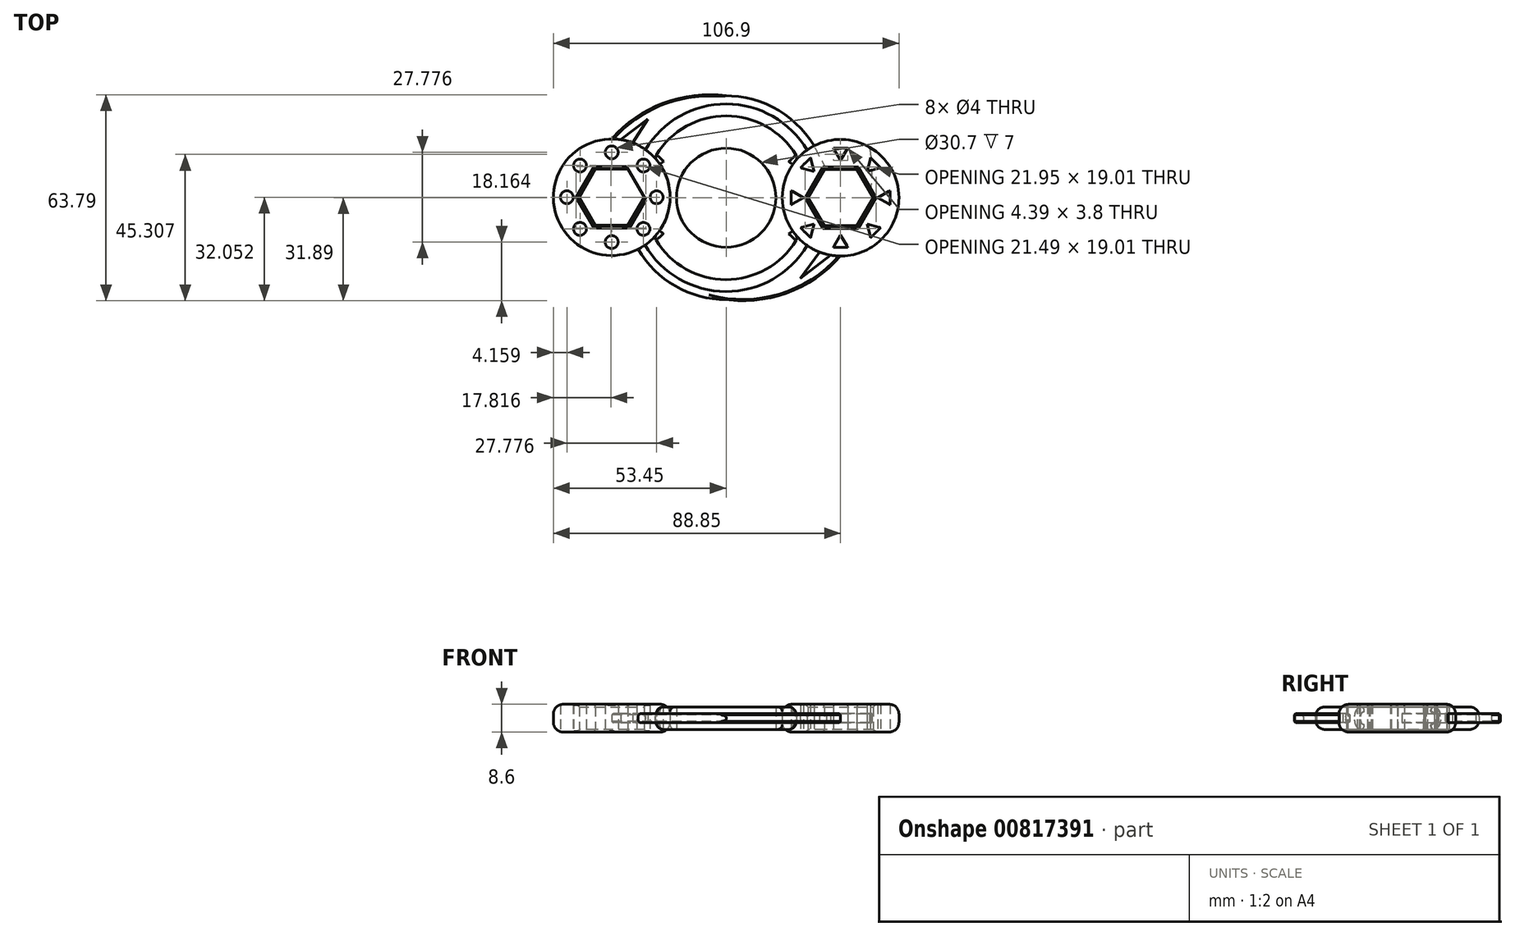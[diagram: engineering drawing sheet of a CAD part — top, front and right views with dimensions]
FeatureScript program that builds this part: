
annotation { "Feature Type Name" : "Feature", "Feature Type Description" : "" }
export const myFeature = defineFeature(function(context is Context, id is Id, definition is map)
    precondition{}
    {
        {
            var Q0;
            Q0=qCreatedBy(makeId("Top.planeOp"),FACE);
            var sketch = newSketch(context, id + "F0", { "sketchPlane" : qUnion([Q0])});
            skCircle(sketch, "E0", {"center": v(0, 0) * mm, "radius": 15.35 * mm});
            skCircle(sketch, "E1", {"center": v(0, 0) * mm, "radius": 25.35 * mm});
            skCircle(sketch, "E2", {"center": v(-35.4, 0.16) * mm, "radius": 10.05 * mm, "construction": true});
            skLineSegment(sketch, "E3.0", {"start": v(-45.45, 0.16) * mm, "end": v(-40.43, -8.54) * mm});
            skLineSegment(sketch, "E3.1", {"start": v(-40.43, 8.87) * mm, "end": v(-45.45, 0.16) * mm});
            skLineSegment(sketch, "E3.3", {"start": v(-25.35, 0.16) * mm, "end": v(-30.38, 8.87) * mm});
            skLineSegment(sketch, "E3.4", {"start": v(-25.35, 0.16) * mm, "end": v(-30.38, -8.54) * mm});
            skLineSegment(sketch, "E3.5", {"start": v(-40.43, -8.54) * mm, "end": v(-30.38, -8.54) * mm});
            skCircle(sketch, "E4.cCircle", {"center": v(35.4, 0) * mm, "radius": 10.05 * mm, "construction": true});
            skLineSegment(sketch, "E4.0", {"start": v(25.35, 0) * mm, "end": v(30.37, 8.7) * mm});
            skLineSegment(sketch, "E4.1", {"start": v(30.38, 8.7) * mm, "end": v(40.42, 8.7) * mm});
            skLineSegment(sketch, "E4.2", {"start": v(40.42, 8.7) * mm, "end": v(45.45, 0) * mm});
            skLineSegment(sketch, "E4.3", {"start": v(45.45, 0) * mm, "end": v(40.43, -8.7) * mm});
            skLineSegment(sketch, "E4.4", {"start": v(40.43, -8.7) * mm, "end": v(30.38, -8.7) * mm});
            skLineSegment(sketch, "E4.5", {"start": v(30.37, -8.7) * mm, "end": v(25.35, 0) * mm});
            skCircle(sketch, "E5", {"center": v(-35.4, 0.16) * mm, "radius": 18.05 * mm});
            skCircle(sketch, "E6", {"center": v(35.4, 0) * mm, "radius": 18.05 * mm});
            skCircle(sketch, "E7", {"center": v(0, 0) * mm, "radius": 31.56 * mm});
            skCircle(sketch, "E8", {"center": v(0, 0) * mm, "radius": 29.06 * mm});
            skLineSegment(sketch, "E9", {"start": v(-40.43, 8.87) * mm, "end": v(-30.38, 8.87) * mm});
            skCircle(sketch, "E10", {"center": v(-35.4, 0.16) * mm, "radius": 14.05 * mm, "construction": true});
            skCircle(sketch, "E11", {"center": v(35.4, 0) * mm, "radius": 14.05 * mm, "construction": true});
            skLineSegment(sketch, "E12.bottom", {"start": v(35.4, 14.05) * mm, "end": v(-35.4, 14.05) * mm, "construction": true});
            skLineSegment(sketch, "E12.top", {"start": v(35.4, -14.05) * mm, "end": v(-35.4, -14.05) * mm, "construction": true});
            skLineSegment(sketch, "E12.left", {"start": v(35.4, 14.05) * mm, "end": v(35.4, -14.05) * mm, "construction": true});
            skLineSegment(sketch, "E12.right", {"start": v(-35.4, 14.05) * mm, "end": v(-35.4, -14.05) * mm, "construction": true});
            skPoint(sketch, "E12.cornerSnap0", {"position": v(35.4, 8.7) * mm});
            skCircle(sketch, "E13", {"center": v(-35.4, 14.05) * mm, "radius": 2 * mm});
            skCircle(sketch, "E14.1.0", {"center": v(-45.22, 9.98) * mm, "radius": 2 * mm});
            skCircle(sketch, "E14.2.0", {"center": v(-49.3, 0.16) * mm, "radius": 2 * mm});
            skCircle(sketch, "E14.3.0", {"center": v(-45.23, -9.66) * mm, "radius": 2 * mm});
            skCircle(sketch, "E14.4.0", {"center": v(-35.4, -13.73) * mm, "radius": 2 * mm});
            skCircle(sketch, "E14.5.0", {"center": v(-25.58, -9.66) * mm, "radius": 2 * mm});
            skCircle(sketch, "E14.6.0", {"center": v(-21.51, 0.16) * mm, "radius": 2 * mm});
            skCircle(sketch, "E14.7.0", {"center": v(-25.58, 9.98) * mm, "radius": 2 * mm});
            skCircle(sketch, "E15.cCircle", {"center": v(35.4, 14.05) * mm, "radius": 1.27 * mm, "construction": true});
            skLineSegment(sketch, "E15.0", {"start": v(33.2, 15.32) * mm, "end": v(37.6, 15.32) * mm});
            skLineSegment(sketch, "E15.1", {"start": v(37.6, 15.32) * mm, "end": v(35.4, 11.52) * mm});
            skLineSegment(sketch, "E15.2", {"start": v(35.4, 11.52) * mm, "end": v(33.2, 15.32) * mm});
            skPoint(sketch, "E15.0.midPoint", {"position": v(35.4, 15.32) * mm});
            skLineSegment(sketch, "E16.1.0", {"start": v(23.02, 9.28) * mm, "end": v(26.12, 12.38) * mm});
            skLineSegment(sketch, "E16.1.1", {"start": v(27.26, 8.14) * mm, "end": v(23.02, 9.28) * mm});
            skLineSegment(sketch, "E16.1.2", {"start": v(26.12, 12.38) * mm, "end": v(27.26, 8.14) * mm});
            skCircle(sketch, "E16.1.3", {"center": v(25.47, 9.93) * mm, "radius": 1.27 * mm, "construction": true});
            skLineSegment(sketch, "E16.2.0", {"start": v(20.08, -2.2) * mm, "end": v(20.08, 2.2) * mm});
            skLineSegment(sketch, "E16.2.1", {"start": v(23.88, 0) * mm, "end": v(20.08, -2.2) * mm});
            skLineSegment(sketch, "E16.2.2", {"start": v(20.08, 2.2) * mm, "end": v(23.88, 0) * mm});
            skCircle(sketch, "E16.2.3", {"center": v(21.35, 0) * mm, "radius": 1.27 * mm, "construction": true});
            skLineSegment(sketch, "E16.3.0", {"start": v(26.12, -12.38) * mm, "end": v(23.02, -9.28) * mm});
            skLineSegment(sketch, "E16.3.1", {"start": v(27.26, -8.14) * mm, "end": v(26.12, -12.38) * mm});
            skLineSegment(sketch, "E16.3.2", {"start": v(23.02, -9.28) * mm, "end": v(27.26, -8.14) * mm});
            skCircle(sketch, "E16.3.3", {"center": v(25.47, -9.93) * mm, "radius": 1.27 * mm, "construction": true});
            skLineSegment(sketch, "E16.4.0", {"start": v(37.6, -15.32) * mm, "end": v(33.2, -15.32) * mm});
            skLineSegment(sketch, "E16.4.1", {"start": v(35.4, -11.52) * mm, "end": v(37.6, -15.32) * mm});
            skLineSegment(sketch, "E16.4.2", {"start": v(33.2, -15.32) * mm, "end": v(35.4, -11.52) * mm});
            skCircle(sketch, "E16.4.3", {"center": v(35.4, -14.05) * mm, "radius": 1.27 * mm, "construction": true});
            skLineSegment(sketch, "E16.5.0", {"start": v(47.78, -9.28) * mm, "end": v(44.68, -12.38) * mm});
            skLineSegment(sketch, "E16.5.1", {"start": v(43.54, -8.14) * mm, "end": v(47.78, -9.28) * mm});
            skLineSegment(sketch, "E16.5.2", {"start": v(44.68, -12.38) * mm, "end": v(43.54, -8.14) * mm});
            skCircle(sketch, "E16.5.3", {"center": v(45.33, -9.93) * mm, "radius": 1.27 * mm, "construction": true});
            skLineSegment(sketch, "E16.6.0", {"start": v(50.72, 2.2) * mm, "end": v(50.72, -2.2) * mm});
            skLineSegment(sketch, "E16.6.1", {"start": v(46.92, 0) * mm, "end": v(50.72, 2.2) * mm});
            skLineSegment(sketch, "E16.6.2", {"start": v(50.72, -2.2) * mm, "end": v(46.92, 0) * mm});
            skCircle(sketch, "E16.6.3", {"center": v(49.45, 0) * mm, "radius": 1.27 * mm, "construction": true});
            skLineSegment(sketch, "E16.7.0", {"start": v(44.68, 12.38) * mm, "end": v(47.78, 9.28) * mm});
            skLineSegment(sketch, "E16.7.1", {"start": v(43.54, 8.14) * mm, "end": v(44.68, 12.38) * mm});
            skLineSegment(sketch, "E16.7.2", {"start": v(47.78, 9.28) * mm, "end": v(43.54, 8.14) * mm});
            skCircle(sketch, "E16.7.3", {"center": v(45.33, 9.93) * mm, "radius": 1.27 * mm, "construction": true});
            skCircle(sketch, "E17", {"center": v(-5.27, -8.1) * mm, "radius": 40 * mm});
            skPoint(sketch, "E17.first.point", {"position": v(-35.4, 18.21) * mm});
            skPoint(sketch, "E17.second.point", {"position": v(0, 31.56) * mm});
            skPoint(sketch, "E17.third.point", {"position": v(-25.3, 26.53) * mm});
            skCircle(sketch, "E18", {"center": v(5.14, 8.11) * mm, "radius": 40 * mm});
            skPoint(sketch, "E18.first.point", {"position": v(35.4, -18.05) * mm});
            skPoint(sketch, "E18.first.point.positionSnap0", {"position": v(35.4, -15.32) * mm});
            skPoint(sketch, "E18.second.point", {"position": v(0, -31.56) * mm});
            skPoint(sketch, "E18.second.point.positionSnap0", {"position": v(0, -14.05) * mm});
            skPoint(sketch, "E18.third.point", {"position": v(-8.62, 45.67) * mm});
            skLineSegment(sketch, "E19", {"start": v(-32.58, 18) * mm, "end": v(-24.21, 24.34) * mm});
            skLineSegment(sketch, "E20", {"start": v(-24.21, 24.34) * mm, "end": v(-28.93, 17.01) * mm});
            skLineSegment(sketch, "E21", {"start": v(28.9, -16.84) * mm, "end": v(22.96, -24.97) * mm});
            skLineSegment(sketch, "E22", {"start": v(22.96, -24.97) * mm, "end": v(32.33, -17.79) * mm});
            skSolve(sketch);
        }
        {
            var Q0;
            {var subQ0=sQuery(id+"F0.wireOp",EDGE,"E7");var subQ4=sQuery(id+"F0.wireOp",EDGE,"E5");var subQ5=makeQuery(id+"F0.imprint","INTERSECT",VERTEX,{"disambiguationData":[OD(0.0)],"derivedFrom":[subQ4,subQ0]});Q0=makeQuery(id+"F0.imprint","IMPRINT",FACE,{"disambiguationData":[TD([[makeQuery(id+"F0.imprint","IMPRINT",EDGE,{"disambiguationData":[TD([[subQ5,-1.0]])],"derivedFrom":subQ4}),1.0]])]});}
            var Q1;
            {var subQ0=sQuery(id+"F0.wireOp",EDGE,"E3.4");Q1=makeQuery(id+"F0.imprint","IMPRINT",FACE,{"disambiguationData":[TD([[makeQuery(id+"F0.imprint","IMPRINT",EDGE,{"derivedFrom":subQ0}),1.0]])]});}
            var Q2;
            {var subQ0=sQuery(id+"F0.wireOp",EDGE,"E5");var subQ1=sQuery(id+"F0.wireOp",EDGE,"E1");var subQ2=makeQuery(id+"F0.imprint","INTERSECT",VERTEX,{"disambiguationData":[OD(0.0)],"derivedFrom":[subQ1,subQ0]});Q2=makeQuery(id+"F0.imprint","IMPRINT",FACE,{"disambiguationData":[TD([[makeQuery(id+"F0.imprint","IMPRINT",EDGE,{"disambiguationData":[TD([[subQ2,-1.0]])],"derivedFrom":subQ0}),1.0]])]});}
            var Q3;
            {var subQ0=sQuery(id+"F0.wireOp",EDGE,"E7");var subQ5=sQuery(id+"F0.wireOp",EDGE,"E5");var subQ6=makeQuery(id+"F0.imprint","INTERSECT",VERTEX,{"disambiguationData":[OD(0.0)],"derivedFrom":[subQ5,subQ0]});Q3=makeQuery(id+"F0.imprint","IMPRINT",FACE,{"disambiguationData":[TD([[makeQuery(id+"F0.imprint","IMPRINT",EDGE,{"disambiguationData":[TD([[subQ6,1.0]])],"derivedFrom":subQ5}),1.0]])]});}
            var Q4;
            {var subQ2=sQuery(id+"F0.wireOp",EDGE,"E5");var subQ5=makeQuery(id+"F0.imprint","INTERSECT",VERTEX,{"derivedFrom":[sQuery(id+"F0.wireOp",EDGE,"E0"),subQ2]});Q4=makeQuery(id+"F0.imprint","IMPRINT",FACE,{"disambiguationData":[TD([[makeQuery(id+"F0.imprint","IMPRINT",EDGE,{"disambiguationData":[TD([[subQ5,-1.0]])],"derivedFrom":subQ2}),1.0]])]});}
            var Q5;
            {var subQ2=sQuery(id+"F0.wireOp",EDGE,"E6");var subQ5=makeQuery(id+"F0.imprint","INTERSECT",VERTEX,{"derivedFrom":[sQuery(id+"F0.wireOp",EDGE,"E0"),subQ2]});Q5=makeQuery(id+"F0.imprint","IMPRINT",FACE,{"disambiguationData":[TD([[makeQuery(id+"F0.imprint","IMPRINT",EDGE,{"disambiguationData":[TD([[subQ5,1.0]])],"derivedFrom":subQ2}),1.0]])]});}
            var Q6;
            {var subQ0=sQuery(id+"F0.wireOp",EDGE,"E5");var subQ1=sQuery(id+"F0.wireOp",EDGE,"E1");var subQ2=makeQuery(id+"F0.imprint","INTERSECT",VERTEX,{"disambiguationData":[OD(1.0)],"derivedFrom":[subQ1,subQ0]});Q6=makeQuery(id+"F0.imprint","IMPRINT",FACE,{"disambiguationData":[TD([[makeQuery(id+"F0.imprint","IMPRINT",EDGE,{"disambiguationData":[TD([[subQ2,1.0]])],"derivedFrom":subQ0}),1.0]])]});}
            var Q7;
            {var subQ1=sQuery(id+"F0.wireOp",EDGE,"E4.2");Q7=makeQuery(id+"F0.imprint","IMPRINT",FACE,{"disambiguationData":[TD([[makeQuery(id+"F0.imprint","IMPRINT",EDGE,{"derivedFrom":subQ1}),1.0]])]});}
            var Q8;
            {var subQ5=sQuery(id+"F0.wireOp",EDGE,"E4.5");Q8=makeQuery(id+"F0.imprint","IMPRINT",FACE,{"disambiguationData":[TD([[makeQuery(id+"F0.imprint","IMPRINT",EDGE,{"derivedFrom":subQ5}),1.0]])]});}
            var Q9;
            {var subQ0=sQuery(id+"F0.wireOp",EDGE,"E7");var subQ5=sQuery(id+"F0.wireOp",EDGE,"E6");var subQ6=makeQuery(id+"F0.imprint","INTERSECT",VERTEX,{"disambiguationData":[OD(1.0)],"derivedFrom":[subQ5,subQ0]});Q9=makeQuery(id+"F0.imprint","IMPRINT",FACE,{"disambiguationData":[TD([[makeQuery(id+"F0.imprint","IMPRINT",EDGE,{"disambiguationData":[TD([[subQ6,1.0]])],"derivedFrom":subQ5}),1.0]])]});}
            var Q10;
            {var subQ0=sQuery(id+"F0.wireOp",EDGE,"E7");var subQ5=sQuery(id+"F0.wireOp",EDGE,"E6");var subQ6=makeQuery(id+"F0.imprint","INTERSECT",VERTEX,{"disambiguationData":[OD(0.0)],"derivedFrom":[subQ5,subQ0]});Q10=makeQuery(id+"F0.imprint","IMPRINT",FACE,{"disambiguationData":[TD([[makeQuery(id+"F0.imprint","IMPRINT",EDGE,{"disambiguationData":[TD([[subQ6,-1.0]])],"derivedFrom":subQ5}),1.0]])]});}
            var Q11;
            {var subQ6=sQuery(id+"F0.wireOp",EDGE,"E4.0");Q11=makeQuery(id+"F0.imprint","IMPRINT",FACE,{"disambiguationData":[TD([[makeQuery(id+"F0.imprint","IMPRINT",EDGE,{"derivedFrom":subQ6}),1.0]])]});}
            var Q12;
            {var subQ1=sQuery(id+"F0.wireOp",EDGE,"E2");var subQ3=sQuery(id+"F0.wireOp",EDGE,"E8");var subQ4=makeQuery(id+"F0.imprint","INTERSECT",VERTEX,{"disambiguationData":[OD(1.0)],"derivedFrom":[subQ1,subQ3]});Q12=makeQuery(id+"F0.imprint","IMPRINT",FACE,{"disambiguationData":[TD([[makeQuery(id+"F0.imprint","IMPRINT",EDGE,{"disambiguationData":[TD([[subQ4,1.0]])],"derivedFrom":subQ3}),1.0]])]});}
            var Q13;
            {var subQ0=sQuery(id+"F0.wireOp",EDGE,"E7");var subQ5=sQuery(id+"F0.wireOp",EDGE,"E5");var subQ6=makeQuery(id+"F0.imprint","INTERSECT",VERTEX,{"disambiguationData":[OD(1.0)],"derivedFrom":[subQ5,subQ0]});Q13=makeQuery(id+"F0.imprint","IMPRINT",FACE,{"disambiguationData":[TD([[makeQuery(id+"F0.imprint","IMPRINT",EDGE,{"disambiguationData":[TD([[subQ6,-1.0]])],"derivedFrom":subQ5}),1.0]])]});}
            var Q14;
            {var subQ1=sQuery(id+"F0.wireOp",EDGE,"E2");var subQ3=sQuery(id+"F0.wireOp",EDGE,"E8");var subQ4=makeQuery(id+"F0.imprint","INTERSECT",VERTEX,{"disambiguationData":[OD(1.0)],"derivedFrom":[subQ1,subQ3]});Q14=makeQuery(id+"F0.imprint","IMPRINT",FACE,{"disambiguationData":[TD([[makeQuery(id+"F0.imprint","IMPRINT",EDGE,{"disambiguationData":[TD([[subQ4,1.0]])],"derivedFrom":subQ3}),-1.0]])]});}
            var Q15;
            {var subQ0=sQuery(id+"F0.wireOp",EDGE,"E3.1");Q15=makeQuery(id+"F0.imprint","IMPRINT",FACE,{"disambiguationData":[TD([[makeQuery(id+"F0.imprint","IMPRINT",EDGE,{"derivedFrom":subQ0}),-1.0]])]});}
            var Q16;
            {var subQ0=sQuery(id+"F0.wireOp",EDGE,"E3.0");Q16=makeQuery(id+"F0.imprint","IMPRINT",FACE,{"disambiguationData":[TD([[makeQuery(id+"F0.imprint","IMPRINT",EDGE,{"derivedFrom":subQ0}),-1.0]])]});}
            var Q17;
            {var subQ0=sQuery(id+"F0.wireOp",EDGE,"E3.5");Q17=makeQuery(id+"F0.imprint","IMPRINT",FACE,{"disambiguationData":[TD([[makeQuery(id+"F0.imprint","IMPRINT",EDGE,{"derivedFrom":subQ0}),-1.0]])]});}
            var Q18;
            {var subQ0=sQuery(id+"F0.wireOp",EDGE,"mRkxw26x-I3Gl-08el-Mtzy-OSO2PS5uUvGy");Q18=makeQuery(id+"F0.imprint","IMPRINT",FACE,{"disambiguationData":[TD([[makeQuery(id+"F0.imprint","IMPRINT",EDGE,{"derivedFrom":subQ0}),1.0]])]});}
            var Q19;
            {var subQ0=sQuery(id+"F0.wireOp",EDGE,"E9");Q19=makeQuery(id+"F0.imprint","IMPRINT",FACE,{"disambiguationData":[TD([[makeQuery(id+"F0.imprint","IMPRINT",EDGE,{"derivedFrom":subQ0}),1.0]])]});}
            var Q20;
            {var subQ0=sQuery(id+"F0.wireOp",EDGE,"E8");var subQ1=sQuery(id+"F0.wireOp",EDGE,"E2");var subQ2=makeQuery(id+"F0.imprint","INTERSECT",VERTEX,{"disambiguationData":[OD(0.0)],"derivedFrom":[subQ1,subQ0]});Q20=makeQuery(id+"F0.imprint","IMPRINT",FACE,{"disambiguationData":[TD([[makeQuery(id+"F0.imprint","IMPRINT",EDGE,{"disambiguationData":[TD([[subQ2,-1.0]])],"derivedFrom":subQ1}),1.0]])]});}
            var Q21;
            {var subQ1=sQuery(id+"F0.wireOp",EDGE,"E2");var subQ3=sQuery(id+"F0.wireOp",EDGE,"E8");var subQ4=makeQuery(id+"F0.imprint","INTERSECT",VERTEX,{"disambiguationData":[OD(0.0)],"derivedFrom":[subQ1,subQ3]});Q21=makeQuery(id+"F0.imprint","IMPRINT",FACE,{"disambiguationData":[TD([[makeQuery(id+"F0.imprint","IMPRINT",EDGE,{"disambiguationData":[TD([[subQ4,-1.0]])],"derivedFrom":subQ3}),1.0]])]});}
            var Q22;
            {var subQ5=sQuery(id+"F0.wireOp",EDGE,"E13");var subQ6=sQuery(id+"F0.wireOp",EDGE,"E10");var subQ7=makeQuery(id+"F0.imprint","INTERSECT",VERTEX,{"disambiguationData":[OD(1.0)],"derivedFrom":[subQ6,subQ5]});Q22=makeQuery(id+"F0.imprint","IMPRINT",FACE,{"disambiguationData":[TD([[makeQuery(id+"F0.imprint","IMPRINT",EDGE,{"disambiguationData":[TD([[subQ7,-1.0]])],"derivedFrom":subQ6}),1.0]])]});}
            var Q23;
            {var subQ0=sQuery(id+"F0.wireOp",EDGE,"E1");var subQ2=sQuery(id+"F0.wireOp",EDGE,"E11");var subQ3=makeQuery(id+"F0.imprint","INTERSECT",VERTEX,{"disambiguationData":[OD(0.0)],"derivedFrom":[subQ0,subQ2]});Q23=makeQuery(id+"F0.imprint","IMPRINT",FACE,{"disambiguationData":[TD([[makeQuery(id+"F0.imprint","IMPRINT",EDGE,{"disambiguationData":[TD([[subQ3,-1.0]])],"derivedFrom":subQ2}),1.0]])]});}
            var Q24;
            {var subQ0=sQuery(id+"F0.wireOp",EDGE,"E7");var subQ5=sQuery(id+"F0.wireOp",EDGE,"E10");var subQ6=makeQuery(id+"F0.imprint","INTERSECT",VERTEX,{"disambiguationData":[OD(1.0)],"derivedFrom":[subQ0,subQ5]});Q24=makeQuery(id+"F0.imprint","IMPRINT",FACE,{"disambiguationData":[TD([[makeQuery(id+"F0.imprint","IMPRINT",EDGE,{"disambiguationData":[TD([[subQ6,1.0]])],"derivedFrom":subQ5}),1.0]])]});}
            var Q25;
            {var subQ1=sQuery(id+"F0.wireOp",EDGE,"E2");var subQ3=sQuery(id+"F0.wireOp",EDGE,"E8");var subQ4=makeQuery(id+"F0.imprint","INTERSECT",VERTEX,{"disambiguationData":[OD(1.0)],"derivedFrom":[subQ1,subQ3]});Q25=makeQuery(id+"F0.imprint","IMPRINT",FACE,{"disambiguationData":[TD([[makeQuery(id+"F0.imprint","IMPRINT",EDGE,{"disambiguationData":[TD([[subQ4,-1.0]])],"derivedFrom":subQ3}),-1.0]])]});}
            var Q26;
            {var subQ0=sQuery(id+"F0.wireOp",EDGE,"E7");var subQ1=sQuery(id+"F0.wireOp",EDGE,"E2");var subQ2=makeQuery(id+"F0.imprint","INTERSECT",VERTEX,{"derivedFrom":[subQ1,subQ0]});Q26=makeQuery(id+"F0.imprint","IMPRINT",FACE,{"disambiguationData":[TD([[makeQuery(id+"F0.imprint","IMPRINT",EDGE,{"disambiguationData":[TD([[subQ2,1.0]])],"derivedFrom":subQ0}),-1.0]])]});}
            var Q27;
            {var subQ0=sQuery(id+"F0.wireOp",EDGE,"E12.bottom");var subQ1=sQuery(id+"F0.wireOp",EDGE,"E7");var subQ2=makeQuery(id+"F0.imprint","INTERSECT",VERTEX,{"disambiguationData":[OD(1.0)],"derivedFrom":[subQ1,subQ0]});Q27=makeQuery(id+"F0.imprint","IMPRINT",FACE,{"disambiguationData":[TD([[makeQuery(id+"F0.imprint","IMPRINT",EDGE,{"disambiguationData":[TD([[subQ2,-1.0]])],"derivedFrom":subQ1}),-1.0]])]});}
            var Q28;
            {var subQ0=sQuery(id+"F0.wireOp",EDGE,"E8");var subQ1=sQuery(id+"F0.wireOp",EDGE,"E2");var subQ2=makeQuery(id+"F0.imprint","INTERSECT",VERTEX,{"disambiguationData":[OD(0.0)],"derivedFrom":[subQ1,subQ0]});Q28=makeQuery(id+"F0.imprint","IMPRINT",FACE,{"disambiguationData":[TD([[makeQuery(id+"F0.imprint","IMPRINT",EDGE,{"disambiguationData":[TD([[subQ2,-1.0]])],"derivedFrom":subQ1}),-1.0]])]});}
            var Q29;
            {var subQ0=sQuery(id+"F0.wireOp",EDGE,"E10");var subQ1=sQuery(id+"F0.wireOp",EDGE,"E7");var subQ2=makeQuery(id+"F0.imprint","INTERSECT",VERTEX,{"disambiguationData":[OD(1.0)],"derivedFrom":[subQ1,subQ0]});Q29=makeQuery(id+"F0.imprint","IMPRINT",FACE,{"disambiguationData":[TD([[makeQuery(id+"F0.imprint","IMPRINT",EDGE,{"disambiguationData":[TD([[subQ2,-1.0]])],"derivedFrom":subQ1}),-1.0]])]});}
            var Q30;
            {var subQ3=sQuery(id+"F0.wireOp",EDGE,"E10");var subQ5=sQuery(id+"F0.wireOp",EDGE,"E1");var subQ10=makeQuery(id+"F0.imprint","INTERSECT",VERTEX,{"disambiguationData":[OD(0.0)],"derivedFrom":[subQ5,subQ3]});Q30=makeQuery(id+"F0.imprint","IMPRINT",FACE,{"disambiguationData":[TD([[makeQuery(id+"F0.imprint","IMPRINT",EDGE,{"disambiguationData":[TD([[subQ10,-1.0]])],"derivedFrom":subQ5}),-1.0]])]});}
            var Q31;
            {var subQ0=sQuery(id+"F0.wireOp",EDGE,"E10");var subQ1=sQuery(id+"F0.wireOp",EDGE,"E1");var subQ2=makeQuery(id+"F0.imprint","INTERSECT",VERTEX,{"disambiguationData":[OD(0.0)],"derivedFrom":[subQ1,subQ0]});Q31=makeQuery(id+"F0.imprint","IMPRINT",FACE,{"disambiguationData":[TD([[makeQuery(id+"F0.imprint","IMPRINT",EDGE,{"disambiguationData":[TD([[subQ2,-1.0]])],"derivedFrom":subQ1}),1.0]])]});}
            var Q32;
            {var subQ0=sQuery(id+"F0.wireOp",EDGE,"E5");var subQ1=sQuery(id+"F0.wireOp",EDGE,"E1");var subQ2=makeQuery(id+"F0.imprint","INTERSECT",VERTEX,{"disambiguationData":[OD(0.0)],"derivedFrom":[subQ1,subQ0]});Q32=makeQuery(id+"F0.imprint","IMPRINT",FACE,{"disambiguationData":[TD([[makeQuery(id+"F0.imprint","IMPRINT",EDGE,{"disambiguationData":[TD([[subQ2,-1.0]])],"derivedFrom":subQ1}),1.0]])]});}
            var Q33;
            {var subQ0=sQuery(id+"F0.wireOp",EDGE,"E11");var subQ5=sQuery(id+"F0.wireOp",EDGE,"E1");var subQ6=makeQuery(id+"F0.imprint","INTERSECT",VERTEX,{"disambiguationData":[OD(0.0)],"derivedFrom":[subQ5,subQ0]});Q33=makeQuery(id+"F0.imprint","IMPRINT",FACE,{"disambiguationData":[TD([[makeQuery(id+"F0.imprint","IMPRINT",EDGE,{"disambiguationData":[TD([[subQ6,-1.0]])],"derivedFrom":subQ5}),-1.0]])]});}
            var Q34;
            {var subQ0=sQuery(id+"F0.wireOp",EDGE,"E11");var subQ1=sQuery(id+"F0.wireOp",EDGE,"E1");var subQ2=makeQuery(id+"F0.imprint","INTERSECT",VERTEX,{"disambiguationData":[OD(0.0)],"derivedFrom":[subQ1,subQ0]});Q34=makeQuery(id+"F0.imprint","IMPRINT",FACE,{"disambiguationData":[TD([[makeQuery(id+"F0.imprint","IMPRINT",EDGE,{"disambiguationData":[TD([[subQ2,-1.0]])],"derivedFrom":subQ1}),1.0]])]});}
            var Q35;
            {var subQ0=sQuery(id+"F0.wireOp",EDGE,"E7");var subQ1=sQuery(id+"F0.wireOp",EDGE,"E6");var subQ5=makeQuery(id+"F0.imprint","INTERSECT",VERTEX,{"disambiguationData":[OD(0.0)],"derivedFrom":[subQ1,subQ0]});Q35=makeQuery(id+"F0.imprint","IMPRINT",FACE,{"disambiguationData":[TD([[makeQuery(id+"F0.imprint","IMPRINT",EDGE,{"disambiguationData":[TD([[subQ5,1.0]])],"derivedFrom":subQ1}),1.0]])]});}
            var Q36;
            {var subQ5=sQuery(id+"F0.wireOp",EDGE,"E4.5");var subQ6=sQuery(id+"F0.wireOp",EDGE,"E4.4");var subQ7=makeQuery(id+"F0.imprint","INTERSECT",VERTEX,{"derivedFrom":[subQ6,subQ5]});Q36=makeQuery(id+"F0.imprint","IMPRINT",FACE,{"disambiguationData":[TD([[makeQuery(id+"F0.imprint","IMPRINT",EDGE,{"disambiguationData":[TD([[subQ7,1.0]])],"derivedFrom":subQ6}),1.0]])]});}
            var Q37;
            {var subQ5=sQuery(id+"F0.wireOp",EDGE,"E1");var subQ7=sQuery(id+"F0.wireOp",EDGE,"E6");var subQ8=makeQuery(id+"F0.imprint","INTERSECT",VERTEX,{"disambiguationData":[OD(1.0)],"derivedFrom":[subQ5,subQ7]});Q37=makeQuery(id+"F0.imprint","IMPRINT",FACE,{"disambiguationData":[TD([[makeQuery(id+"F0.imprint","IMPRINT",EDGE,{"disambiguationData":[TD([[subQ8,-1.0]])],"derivedFrom":subQ5}),-1.0]])]});}
            var Q38;
            {var subQ0=sQuery(id+"F0.wireOp",EDGE,"E12.top");var subQ1=sQuery(id+"F0.wireOp",EDGE,"E7");var subQ2=makeQuery(id+"F0.imprint","INTERSECT",VERTEX,{"disambiguationData":[OD(1.0)],"derivedFrom":[subQ1,subQ0]});Q38=makeQuery(id+"F0.imprint","IMPRINT",FACE,{"disambiguationData":[TD([[makeQuery(id+"F0.imprint","IMPRINT",EDGE,{"disambiguationData":[TD([[subQ2,-1.0]])],"derivedFrom":subQ1}),-1.0]])]});}
            var Q39;
            {var subQ0=sQuery(id+"F0.wireOp",EDGE,"E11");var subQ1=sQuery(id+"F0.wireOp",EDGE,"E7");var subQ2=makeQuery(id+"F0.imprint","INTERSECT",VERTEX,{"disambiguationData":[OD(0.0)],"derivedFrom":[subQ1,subQ0]});Q39=makeQuery(id+"F0.imprint","IMPRINT",FACE,{"disambiguationData":[TD([[makeQuery(id+"F0.imprint","IMPRINT",EDGE,{"disambiguationData":[TD([[subQ2,-1.0]])],"derivedFrom":subQ1}),-1.0]])]});}
            var Q40;
            {var subQ5=sQuery(id+"F0.wireOp",EDGE,"E4.0");var subQ7=sQuery(id+"F0.wireOp",EDGE,"E4.1");var subQ8=makeQuery(id+"F0.imprint","INTERSECT",VERTEX,{"derivedFrom":[subQ5,subQ7]});Q40=makeQuery(id+"F0.imprint","IMPRINT",FACE,{"disambiguationData":[TD([[makeQuery(id+"F0.imprint","IMPRINT",EDGE,{"disambiguationData":[TD([[subQ8,1.0]])],"derivedFrom":subQ5}),1.0]])]});}
            var Q41;
            {var subQ0=sQuery(id+"F0.wireOp",EDGE,"E12.bottom");var subQ1=sQuery(id+"F0.wireOp",EDGE,"E7");var subQ2=makeQuery(id+"F0.imprint","INTERSECT",VERTEX,{"disambiguationData":[OD(1.0)],"derivedFrom":[subQ1,subQ0]});Q41=makeQuery(id+"F0.imprint","IMPRINT",FACE,{"disambiguationData":[TD([[makeQuery(id+"F0.imprint","IMPRINT",EDGE,{"disambiguationData":[TD([[subQ2,-1.0]])],"derivedFrom":subQ1}),1.0]])]});}
            var Q42;
            {var subQ0=sQuery(id+"F0.wireOp",EDGE,"E10");var subQ1=sQuery(id+"F0.wireOp",EDGE,"E7");var subQ2=makeQuery(id+"F0.imprint","INTERSECT",VERTEX,{"disambiguationData":[OD(1.0)],"derivedFrom":[subQ1,subQ0]});Q42=makeQuery(id+"F0.imprint","IMPRINT",FACE,{"disambiguationData":[TD([[makeQuery(id+"F0.imprint","IMPRINT",EDGE,{"disambiguationData":[TD([[subQ2,-1.0]])],"derivedFrom":subQ1}),1.0]])]});}
            var Q43;
            {var subQ0=sQuery(id+"F0.wireOp",EDGE,"E12.top");var subQ1=sQuery(id+"F0.wireOp",EDGE,"E7");var subQ2=makeQuery(id+"F0.imprint","INTERSECT",VERTEX,{"disambiguationData":[OD(1.0)],"derivedFrom":[subQ1,subQ0]});Q43=makeQuery(id+"F0.imprint","IMPRINT",FACE,{"disambiguationData":[TD([[makeQuery(id+"F0.imprint","IMPRINT",EDGE,{"disambiguationData":[TD([[subQ2,-1.0]])],"derivedFrom":subQ1}),1.0]])]});}
            var Q44;
            {var subQ0=sQuery(id+"F0.wireOp",EDGE,"E11");var subQ1=sQuery(id+"F0.wireOp",EDGE,"E7");var subQ2=makeQuery(id+"F0.imprint","INTERSECT",VERTEX,{"disambiguationData":[OD(0.0)],"derivedFrom":[subQ1,subQ0]});Q44=makeQuery(id+"F0.imprint","IMPRINT",FACE,{"disambiguationData":[TD([[makeQuery(id+"F0.imprint","IMPRINT",EDGE,{"disambiguationData":[TD([[subQ2,-1.0]])],"derivedFrom":subQ1}),1.0]])]});}
            var Q45;
            {var subQ1=sQuery(id+"F0.wireOp",EDGE,"E8");var subQ5=sQuery(id+"F0.wireOp",EDGE,"E4.0");var subQ6=makeQuery(id+"F0.imprint","INTERSECT",VERTEX,{"derivedFrom":[subQ5,subQ1]});Q45=makeQuery(id+"F0.imprint","IMPRINT",FACE,{"disambiguationData":[TD([[makeQuery(id+"F0.imprint","IMPRINT",EDGE,{"disambiguationData":[TD([[subQ6,-1.0]])],"derivedFrom":subQ1}),1.0]])]});}
            var Q46;
            {var subQ8=sQuery(id+"F0.wireOp",EDGE,"E1");var subQ11=sQuery(id+"F0.wireOp",EDGE,"E16.1.0");var subQ12=makeQuery(id+"F0.imprint","INTERSECT",VERTEX,{"derivedFrom":[subQ8,subQ11]});Q46=makeQuery(id+"F0.imprint","IMPRINT",FACE,{"disambiguationData":[TD([[makeQuery(id+"F0.imprint","IMPRINT",EDGE,{"disambiguationData":[TD([[subQ12,-1.0]])],"derivedFrom":subQ8}),-1.0]])]});}
            var Q47;
            {var subQ0=sQuery(id+"F0.wireOp",EDGE,"E8");var subQ1=sQuery(id+"F0.wireOp",EDGE,"E4.5");var subQ2=makeQuery(id+"F0.imprint","INTERSECT",VERTEX,{"derivedFrom":[subQ1,subQ0]});Q47=makeQuery(id+"F0.imprint","IMPRINT",FACE,{"disambiguationData":[TD([[makeQuery(id+"F0.imprint","IMPRINT",EDGE,{"disambiguationData":[TD([[subQ2,1.0]])],"derivedFrom":subQ0}),1.0]])]});}
            var Q48;
            {var subQ0=sQuery(id+"F0.wireOp",EDGE,"E16.3.2");var subQ1=sQuery(id+"F0.wireOp",EDGE,"E1");var subQ2=makeQuery(id+"F0.imprint","INTERSECT",VERTEX,{"derivedFrom":[subQ1,subQ0]});Q48=makeQuery(id+"F0.imprint","IMPRINT",FACE,{"disambiguationData":[TD([[makeQuery(id+"F0.imprint","IMPRINT",EDGE,{"disambiguationData":[TD([[subQ2,-1.0]])],"derivedFrom":subQ1}),-1.0]])]});}
            var Q49;
            {var subQ0=sQuery(id+"F0.wireOp",EDGE,"E16.5.0");Q49=makeQuery(id+"F0.imprint","IMPRINT",FACE,{"disambiguationData":[TD([[makeQuery(id+"F0.imprint","IMPRINT",EDGE,{"derivedFrom":subQ0}),1.0]])]});}
            var Q50;
            {var subQ1=sQuery(id+"F0.wireOp",EDGE,"E10");var subQ9=sQuery(id+"F0.wireOp",EDGE,"E17");var subQ17=makeQuery(id+"F0.imprint","INTERSECT",VERTEX,{"disambiguationData":[OD(0.0)],"derivedFrom":[subQ1,subQ9]});Q50=makeQuery(id+"F0.imprint","IMPRINT",FACE,{"disambiguationData":[TD([[makeQuery(id+"F0.imprint","IMPRINT",EDGE,{"disambiguationData":[TD([[subQ17,-1.0]])],"derivedFrom":subQ1}),1.0]])]});}
            var Q51;
            {var subQ5=sQuery(id+"F0.wireOp",EDGE,"E5");var subQ7=sQuery(id+"F0.wireOp",EDGE,"E17");var subQ11=makeQuery(id+"F0.imprint","INTERSECT",VERTEX,{"disambiguationData":[OD(1.0)],"derivedFrom":[subQ5,subQ7]});Q51=makeQuery(id+"F0.imprint","IMPRINT",FACE,{"disambiguationData":[TD([[makeQuery(id+"F0.imprint","IMPRINT",EDGE,{"disambiguationData":[TD([[subQ11,-1.0]])],"derivedFrom":subQ5}),1.0]])]});}
            var Q52;
            {var subQ3=sQuery(id+"F0.wireOp",EDGE,"E18");var subQ6=sQuery(id+"F0.wireOp",EDGE,"E6");var subQ10=makeQuery(id+"F0.imprint","INTERSECT",VERTEX,{"disambiguationData":[OD(1.0)],"derivedFrom":[subQ6,subQ3]});Q52=makeQuery(id+"F0.imprint","IMPRINT",FACE,{"disambiguationData":[TD([[makeQuery(id+"F0.imprint","IMPRINT",EDGE,{"disambiguationData":[TD([[subQ10,1.0]])],"derivedFrom":subQ6}),1.0]])]});}
            var Q53;
            {var subQ1=sQuery(id+"F0.wireOp",EDGE,"E11");var subQ6=sQuery(id+"F0.wireOp",EDGE,"E1");var subQ9=makeQuery(id+"F0.imprint","INTERSECT",VERTEX,{"disambiguationData":[OD(0.0)],"derivedFrom":[subQ6,subQ1]});Q53=makeQuery(id+"F0.imprint","IMPRINT",FACE,{"disambiguationData":[TD([[makeQuery(id+"F0.imprint","IMPRINT",EDGE,{"disambiguationData":[TD([[subQ9,1.0]])],"derivedFrom":subQ1}),1.0]])]});}
            var Q54;
            {var subQ0=sQuery(id+"F0.wireOp",EDGE,"E11");var subQ1=sQuery(id+"F0.wireOp",EDGE,"E1");var subQ2=makeQuery(id+"F0.imprint","INTERSECT",VERTEX,{"disambiguationData":[OD(1.0)],"derivedFrom":[subQ1,subQ0]});Q54=makeQuery(id+"F0.imprint","IMPRINT",FACE,{"disambiguationData":[TD([[makeQuery(id+"F0.imprint","IMPRINT",EDGE,{"disambiguationData":[TD([[subQ2,-1.0]])],"derivedFrom":subQ0}),1.0]])]});}
            var Q55;
            {var subQ0=sQuery(id+"F0.wireOp",EDGE,"E8");var subQ1=sQuery(id+"F0.wireOp",EDGE,"E2");var subQ2=makeQuery(id+"F0.imprint","INTERSECT",VERTEX,{"disambiguationData":[OD(1.0)],"derivedFrom":[subQ1,subQ0]});Q55=makeQuery(id+"F0.imprint","IMPRINT",FACE,{"disambiguationData":[TD([[makeQuery(id+"F0.imprint","IMPRINT",EDGE,{"disambiguationData":[TD([[subQ2,-1.0]])],"derivedFrom":subQ1}),-1.0]])]});}
            var Q56;
            {var subQ0=sQuery(id+"F0.wireOp",EDGE,"E12.top");var subQ1=sQuery(id+"F0.wireOp",EDGE,"E5");var subQ2=makeQuery(id+"F0.imprint","INTERSECT",VERTEX,{"derivedFrom":[subQ1,subQ0]});Q56=makeQuery(id+"F0.imprint","IMPRINT",FACE,{"disambiguationData":[TD([[makeQuery(id+"F0.imprint","IMPRINT",EDGE,{"disambiguationData":[TD([[subQ2,-1.0]])],"derivedFrom":subQ1}),1.0]])]});}
            var Q57;
            {var subQ1=sQuery(id+"F0.wireOp",EDGE,"E2");var subQ3=sQuery(id+"F0.wireOp",EDGE,"E18");var subQ4=makeQuery(id+"F0.imprint","INTERSECT",VERTEX,{"disambiguationData":[OD(0.0)],"derivedFrom":[subQ1,subQ3]});Q57=makeQuery(id+"F0.imprint","IMPRINT",FACE,{"disambiguationData":[TD([[makeQuery(id+"F0.imprint","IMPRINT",EDGE,{"disambiguationData":[TD([[subQ4,-1.0]])],"derivedFrom":subQ3}),1.0]])]});}
            var Q58;
            {var subQ0=sQuery(id+"F0.wireOp",EDGE,"E18");var subQ1=sQuery(id+"F0.wireOp",EDGE,"E2");var subQ2=makeQuery(id+"F0.imprint","INTERSECT",VERTEX,{"disambiguationData":[OD(0.0)],"derivedFrom":[subQ1,subQ0]});Q58=makeQuery(id+"F0.imprint","IMPRINT",FACE,{"disambiguationData":[TD([[makeQuery(id+"F0.imprint","IMPRINT",EDGE,{"disambiguationData":[TD([[subQ2,-1.0]])],"derivedFrom":subQ1}),-1.0]])]});}
            var Q59;
            {var subQ0=sQuery(id+"F0.wireOp",EDGE,"E12.right");var subQ1=sQuery(id+"F0.wireOp",EDGE,"E2");var subQ2=makeQuery(id+"F0.imprint","INTERSECT",VERTEX,{"disambiguationData":[OD(0.0)],"derivedFrom":[subQ1,subQ0]});Q59=makeQuery(id+"F0.imprint","IMPRINT",FACE,{"disambiguationData":[TD([[makeQuery(id+"F0.imprint","IMPRINT",EDGE,{"disambiguationData":[TD([[subQ2,-1.0]])],"derivedFrom":subQ1}),1.0]])]});}
            var Q60;
            {var subQ0=sQuery(id+"F0.wireOp",EDGE,"E12.bottom");var subQ1=sQuery(id+"F0.wireOp",EDGE,"E6");var subQ2=makeQuery(id+"F0.imprint","INTERSECT",VERTEX,{"derivedFrom":[subQ1,subQ0]});Q60=makeQuery(id+"F0.imprint","IMPRINT",FACE,{"disambiguationData":[TD([[makeQuery(id+"F0.imprint","IMPRINT",EDGE,{"disambiguationData":[TD([[subQ2,-1.0]])],"derivedFrom":subQ1}),1.0]])]});}
            var Q61;
            {var subQ5=sQuery(id+"F0.wireOp",EDGE,"E18");var subQ7=sQuery(id+"F0.wireOp",EDGE,"E4.4");var subQ9=makeQuery(id+"F0.imprint","INTERSECT",VERTEX,{"derivedFrom":[subQ7,subQ5]});Q61=makeQuery(id+"F0.imprint","IMPRINT",FACE,{"disambiguationData":[TD([[makeQuery(id+"F0.imprint","IMPRINT",EDGE,{"disambiguationData":[TD([[subQ9,-1.0]])],"derivedFrom":subQ7}),1.0]])]});}
            var Q62;
            {var subQ16=sQuery(id+"F0.wireOp",EDGE,"E4.3");Q62=makeQuery(id+"F0.imprint","IMPRINT",FACE,{"disambiguationData":[TD([[makeQuery(id+"F0.imprint","IMPRINT",EDGE,{"derivedFrom":subQ16}),1.0]])]});}
            var Q63;
            {var subQ0=sQuery(id+"F0.wireOp",EDGE,"E8");var subQ1=sQuery(id+"F0.wireOp",EDGE,"E5");var subQ2=makeQuery(id+"F0.imprint","INTERSECT",VERTEX,{"disambiguationData":[OD(0.0)],"derivedFrom":[subQ1,subQ0]});Q63=makeQuery(id+"F0.imprint","IMPRINT",FACE,{"disambiguationData":[TD([[makeQuery(id+"F0.imprint","IMPRINT",EDGE,{"disambiguationData":[TD([[subQ2,-1.0]])],"derivedFrom":subQ1}),1.0]])]});}
            var Q64;
            {var subQ0=sQuery(id+"F0.wireOp",EDGE,"E12.bottom");var subQ1=sQuery(id+"F0.wireOp",EDGE,"E8");var subQ2=makeQuery(id+"F0.imprint","INTERSECT",VERTEX,{"disambiguationData":[OD(1.0)],"derivedFrom":[subQ1,subQ0]});Q64=makeQuery(id+"F0.imprint","IMPRINT",FACE,{"disambiguationData":[TD([[makeQuery(id+"F0.imprint","IMPRINT",EDGE,{"disambiguationData":[TD([[subQ2,-1.0]])],"derivedFrom":subQ1}),-1.0]])]});}
            var Q65;
            {var subQ0=sQuery(id+"F0.wireOp",EDGE,"E8");var subQ1=sQuery(id+"F0.wireOp",EDGE,"E6");var subQ2=makeQuery(id+"F0.imprint","INTERSECT",VERTEX,{"disambiguationData":[OD(1.0)],"derivedFrom":[subQ1,subQ0]});Q65=makeQuery(id+"F0.imprint","IMPRINT",FACE,{"disambiguationData":[TD([[makeQuery(id+"F0.imprint","IMPRINT",EDGE,{"disambiguationData":[TD([[subQ2,-1.0]])],"derivedFrom":subQ1}),1.0]])]});}
            var Q66;
            {var subQ0=sQuery(id+"F0.wireOp",EDGE,"E16.4.1");var subQ1=sQuery(id+"F0.wireOp",EDGE,"E11");var subQ2=makeQuery(id+"F0.imprint","INTERSECT",VERTEX,{"derivedFrom":[subQ1,subQ0]});Q66=makeQuery(id+"F0.imprint","IMPRINT",FACE,{"disambiguationData":[TD([[makeQuery(id+"F0.imprint","IMPRINT",EDGE,{"disambiguationData":[TD([[subQ2,-1.0]])],"derivedFrom":subQ1}),-1.0]])]});}
            var Q67;
            {var subQ0=sQuery(id+"F0.wireOp",EDGE,"E17");var subQ1=sQuery(id+"F0.wireOp",EDGE,"E8");var subQ2=makeQuery(id+"F0.imprint","INTERSECT",VERTEX,{"disambiguationData":[OD(1.0)],"derivedFrom":[subQ1,subQ0]});Q67=makeQuery(id+"F0.imprint","IMPRINT",FACE,{"disambiguationData":[TD([[makeQuery(id+"F0.imprint","IMPRINT",EDGE,{"disambiguationData":[TD([[subQ2,-1.0]])],"derivedFrom":subQ1}),1.0]])]});}
            var Q68;
            {var subQ0=sQuery(id+"F0.wireOp",EDGE,"E16.3.1");var subQ1=sQuery(id+"F0.wireOp",EDGE,"E11");var subQ2=makeQuery(id+"F0.imprint","INTERSECT",VERTEX,{"derivedFrom":[subQ1,subQ0]});Q68=makeQuery(id+"F0.imprint","IMPRINT",FACE,{"disambiguationData":[TD([[makeQuery(id+"F0.imprint","IMPRINT",EDGE,{"disambiguationData":[TD([[subQ2,-1.0]])],"derivedFrom":subQ1}),1.0]])]});}
            var Q69;
            {var subQ0=sQuery(id+"F0.wireOp",EDGE,"E12.top");var subQ1=sQuery(id+"F0.wireOp",EDGE,"E8");var subQ2=makeQuery(id+"F0.imprint","INTERSECT",VERTEX,{"disambiguationData":[OD(1.0)],"derivedFrom":[subQ1,subQ0]});Q69=makeQuery(id+"F0.imprint","IMPRINT",FACE,{"disambiguationData":[TD([[makeQuery(id+"F0.imprint","IMPRINT",EDGE,{"disambiguationData":[TD([[subQ2,-1.0]])],"derivedFrom":subQ1}),-1.0]])]});}
            var Q70;
            {var subQ5=sQuery(id+"F0.wireOp",EDGE,"E14.3.0");var subQ6=sQuery(id+"F0.wireOp",EDGE,"E10");var subQ7=makeQuery(id+"F0.imprint","INTERSECT",VERTEX,{"disambiguationData":[OD(1.0)],"derivedFrom":[subQ6,subQ5]});Q70=makeQuery(id+"F0.imprint","IMPRINT",FACE,{"disambiguationData":[TD([[makeQuery(id+"F0.imprint","IMPRINT",EDGE,{"disambiguationData":[TD([[subQ7,-1.0]])],"derivedFrom":subQ6}),1.0]])]});}
            var Q71;
            {var subQ3=sQuery(id+"F0.wireOp",EDGE,"E12.right");var subQ5=sQuery(id+"F0.wireOp",EDGE,"E2");var subQ6=makeQuery(id+"F0.imprint","INTERSECT",VERTEX,{"disambiguationData":[OD(1.0)],"derivedFrom":[subQ5,subQ3]});Q71=makeQuery(id+"F0.imprint","IMPRINT",FACE,{"disambiguationData":[TD([[makeQuery(id+"F0.imprint","IMPRINT",EDGE,{"disambiguationData":[TD([[subQ6,-1.0]])],"derivedFrom":subQ5}),-1.0]])]});}
            var Q72;
            {var subQ0=sQuery(id+"F0.wireOp",EDGE,"E18");var subQ1=sQuery(id+"F0.wireOp",EDGE,"E2");var subQ2=makeQuery(id+"F0.imprint","INTERSECT",VERTEX,{"disambiguationData":[OD(0.0)],"derivedFrom":[subQ1,subQ0]});Q72=makeQuery(id+"F0.imprint","IMPRINT",FACE,{"disambiguationData":[TD([[makeQuery(id+"F0.imprint","IMPRINT",EDGE,{"disambiguationData":[TD([[subQ2,-1.0]])],"derivedFrom":subQ1}),1.0]])]});}
            var Q73;
            {var subQ5=sQuery(id+"F0.wireOp",EDGE,"E17");var subQ6=sQuery(id+"F0.wireOp",EDGE,"E5");var subQ7=makeQuery(id+"F0.imprint","INTERSECT",VERTEX,{"disambiguationData":[OD(0.0)],"derivedFrom":[subQ6,subQ5]});Q73=makeQuery(id+"F0.imprint","IMPRINT",FACE,{"disambiguationData":[TD([[makeQuery(id+"F0.imprint","IMPRINT",EDGE,{"disambiguationData":[TD([[subQ7,1.0]])],"derivedFrom":subQ6}),1.0]])]});}
            var Q74;
            Q74=makeQuery(id+"F0.imprint","IMPRINT",FACE,{"disambiguationData":[TD([[makeQuery(id+"F0.imprint","IMPRINT",EDGE,{"derivedFrom":sQuery(id+"F0.wireOp",EDGE,"E16.2.0")}),1.0]])]});
            var Q75;
            {var subQ0=sQuery(id+"F0.wireOp",EDGE,"E8");var subQ1=sQuery(id+"F0.wireOp",EDGE,"E4.0");var subQ2=makeQuery(id+"F0.imprint","INTERSECT",VERTEX,{"derivedFrom":[subQ1,subQ0]});Q75=makeQuery(id+"F0.imprint","IMPRINT",FACE,{"disambiguationData":[TD([[makeQuery(id+"F0.imprint","IMPRINT",EDGE,{"disambiguationData":[TD([[subQ2,-1.0]])],"derivedFrom":subQ1}),1.0]])]});}
            var Q76;
            Q76=makeQuery(id+"F0.imprint","IMPRINT",FACE,{"disambiguationData":[TD([[makeQuery(id+"F0.imprint","IMPRINT",EDGE,{"derivedFrom":sQuery(id+"F0.wireOp",EDGE,"E14.1.0")}),-1.0]])]});
            extrude(context, id + "F1", {"entities" : qUnion([Q0, Q1, Q2, Q3, Q4, Q5, Q6, Q7, Q8, Q9, Q10, Q11, Q12, Q13, Q14, Q15, Q16, Q17, Q18, Q19, Q20, Q21, Q22, Q23, Q24, Q25, Q26, Q27, Q28, Q29, Q30, Q31, Q32, Q33, Q34, Q35, Q36, Q37, Q38, Q39, Q40, Q41, Q42, Q43, Q44, Q45, Q46, Q47, Q48, Q49, Q50, Q51, Q52, Q53, Q54, Q55, Q56, Q57, Q58, Q59, Q60, Q61, Q62, Q63, Q64, Q65, Q66, Q67, Q68, Q69, Q70, Q71, Q72, Q73, Q74, Q75, Q76]), "endBound" : BoundingType.SYMMETRIC, "depth" : 8.6 * mm, "offsetDistance" : 25 * mm});
        }
        {
            var Q0;
            Q0=makeQuery(id+"F0.imprint","IMPRINT",FACE,{"disambiguationData":[TD([[makeQuery(id+"F0.imprint","IMPRINT",EDGE,{"derivedFrom":sQuery(id+"F0.wireOp",EDGE,"E0")}),-1.0]])]});
            var Q1;
            {var subQ6=sQuery(id+"F0.wireOp",EDGE,"E12.bottom");var subQ7=sQuery(id+"F0.wireOp",EDGE,"E0");var subQ8=makeQuery(id+"F0.imprint","INTERSECT",VERTEX,{"disambiguationData":[OD(0.0)],"derivedFrom":[subQ7,subQ6]});Q1=makeQuery(id+"F0.imprint","IMPRINT",FACE,{"disambiguationData":[TD([[makeQuery(id+"F0.imprint","IMPRINT",EDGE,{"disambiguationData":[TD([[subQ8,-1.0]])],"derivedFrom":subQ7}),-1.0]])]});}
            var Q2;
            {var subQ5=sQuery(id+"F0.wireOp",EDGE,"E0");var subQ8=sQuery(id+"F0.wireOp",EDGE,"E12.bottom");var subQ9=makeQuery(id+"F0.imprint","INTERSECT",VERTEX,{"disambiguationData":[OD(1.0)],"derivedFrom":[subQ5,subQ8]});Q2=makeQuery(id+"F0.imprint","IMPRINT",FACE,{"disambiguationData":[TD([[makeQuery(id+"F0.imprint","IMPRINT",EDGE,{"disambiguationData":[TD([[subQ9,1.0]])],"derivedFrom":subQ5}),-1.0]])]});}
            extrude(context, id + "F2", {"entities" : qUnion([Q0, Q1, Q2]), "endBound" : BoundingType.SYMMETRIC, "depth" : 7 * mm, "offsetDistance" : 25 * mm});
        }
        {
            var Q0;
            {var subQ0=sQuery(id+"F0.wireOp",EDGE,"E7");var subQ1=sQuery(id+"F0.wireOp",EDGE,"E5");var subQ2=makeQuery(id+"F0.imprint","INTERSECT",VERTEX,{"disambiguationData":[OD(0.0)],"derivedFrom":[subQ1,subQ0]});Q0=makeQuery(id+"F0.imprint","IMPRINT",FACE,{"disambiguationData":[TD([[makeQuery(id+"F0.imprint","IMPRINT",EDGE,{"disambiguationData":[TD([[subQ2,1.0]])],"derivedFrom":subQ1}),-1.0]])]});}
            var Q1;
            {var subQ0=sQuery(id+"F0.wireOp",EDGE,"E7");var subQ1=sQuery(id+"F0.wireOp",EDGE,"E5");var subQ2=makeQuery(id+"F0.imprint","INTERSECT",VERTEX,{"disambiguationData":[OD(1.0)],"derivedFrom":[subQ1,subQ0]});Q1=makeQuery(id+"F0.imprint","IMPRINT",FACE,{"disambiguationData":[TD([[makeQuery(id+"F0.imprint","IMPRINT",EDGE,{"disambiguationData":[TD([[subQ2,-1.0]])],"derivedFrom":subQ1}),-1.0]])]});}
            var Q2;
            {var subQ1=sQuery(id+"F0.wireOp",EDGE,"E6");var subQ5=sQuery(id+"F0.wireOp",EDGE,"E8");var subQ6=makeQuery(id+"F0.imprint","INTERSECT",VERTEX,{"disambiguationData":[OD(1.0)],"derivedFrom":[subQ1,subQ5]});Q2=makeQuery(id+"F0.imprint","IMPRINT",FACE,{"disambiguationData":[TD([[makeQuery(id+"F0.imprint","IMPRINT",EDGE,{"disambiguationData":[TD([[subQ6,-1.0]])],"derivedFrom":subQ1}),-1.0]])]});}
            var Q3;
            {var subQ0=sQuery(id+"F0.wireOp",EDGE,"E17");var subQ1=sQuery(id+"F0.wireOp",EDGE,"E6");var subQ2=makeQuery(id+"F0.imprint","INTERSECT",VERTEX,{"disambiguationData":[OD(1.0)],"derivedFrom":[subQ1,subQ0]});Q3=makeQuery(id+"F0.imprint","IMPRINT",FACE,{"disambiguationData":[TD([[makeQuery(id+"F0.imprint","IMPRINT",EDGE,{"disambiguationData":[TD([[subQ2,-1.0]])],"derivedFrom":subQ1}),-1.0]])]});}
            var Q4;
            {var subQ0=sQuery(id+"F0.wireOp",EDGE,"E18");var subQ1=sQuery(id+"F0.wireOp",EDGE,"E7");var subQ2=makeQuery(id+"F0.imprint","INTERSECT",VERTEX,{"disambiguationData":[OD(1.0)],"derivedFrom":[subQ1,subQ0]});Q4=makeQuery(id+"F0.imprint","IMPRINT",FACE,{"disambiguationData":[TD([[makeQuery(id+"F0.imprint","IMPRINT",EDGE,{"disambiguationData":[TD([[subQ2,-1.0]])],"derivedFrom":subQ1}),-1.0]])]});}
            var Q5;
            {var subQ0=sQuery(id+"F0.wireOp",EDGE,"E18");var subQ1=sQuery(id+"F0.wireOp",EDGE,"E6");var subQ2=makeQuery(id+"F0.imprint","INTERSECT",VERTEX,{"disambiguationData":[OD(1.0)],"derivedFrom":[subQ1,subQ0]});Q5=makeQuery(id+"F0.imprint","IMPRINT",FACE,{"disambiguationData":[TD([[makeQuery(id+"F0.imprint","IMPRINT",EDGE,{"disambiguationData":[TD([[subQ2,1.0]])],"derivedFrom":subQ1}),-1.0]])]});}
            var Q6;
            {var subQ0=sQuery(id+"F0.wireOp",EDGE,"E17");var subQ1=sQuery(id+"F0.wireOp",EDGE,"E5");var subQ2=makeQuery(id+"F0.imprint","INTERSECT",VERTEX,{"disambiguationData":[OD(0.0)],"derivedFrom":[subQ1,subQ0]});Q6=makeQuery(id+"F0.imprint","IMPRINT",FACE,{"disambiguationData":[TD([[makeQuery(id+"F0.imprint","IMPRINT",EDGE,{"disambiguationData":[TD([[subQ2,1.0]])],"derivedFrom":subQ1}),-1.0]])]});}
            var Q7;
            {var subQ0=sQuery(id+"F0.wireOp",EDGE,"E8");var subQ1=sQuery(id+"F0.wireOp",EDGE,"E5");var subQ2=makeQuery(id+"F0.imprint","INTERSECT",VERTEX,{"disambiguationData":[OD(0.0)],"derivedFrom":[subQ1,subQ0]});Q7=makeQuery(id+"F0.imprint","IMPRINT",FACE,{"disambiguationData":[TD([[makeQuery(id+"F0.imprint","IMPRINT",EDGE,{"disambiguationData":[TD([[subQ2,-1.0]])],"derivedFrom":subQ1}),-1.0]])]});}
            var Q8;
            {var subQ0=sQuery(id+"F0.wireOp",EDGE,"E17");var subQ1=sQuery(id+"F0.wireOp",EDGE,"E7");var subQ2=makeQuery(id+"F0.imprint","INTERSECT",VERTEX,{"disambiguationData":[OD(0.0)],"derivedFrom":[subQ1,subQ0]});Q8=makeQuery(id+"F0.imprint","IMPRINT",FACE,{"disambiguationData":[TD([[makeQuery(id+"F0.imprint","IMPRINT",EDGE,{"disambiguationData":[TD([[subQ2,-1.0]])],"derivedFrom":subQ1}),-1.0]])]});}
            var Q9;
            {var subQ0=sQuery(id+"F0.wireOp",EDGE,"E7");var subQ1=sQuery(id+"F0.wireOp",EDGE,"E6");var subQ2=makeQuery(id+"F0.imprint","INTERSECT",VERTEX,{"disambiguationData":[OD(0.0)],"derivedFrom":[subQ1,subQ0]});Q9=makeQuery(id+"F0.imprint","IMPRINT",FACE,{"disambiguationData":[TD([[makeQuery(id+"F0.imprint","IMPRINT",EDGE,{"disambiguationData":[TD([[subQ2,-1.0]])],"derivedFrom":subQ1}),-1.0]])]});}
            var Q10;
            {var subQ0=sQuery(id+"F0.wireOp",EDGE,"E7");var subQ1=sQuery(id+"F0.wireOp",EDGE,"E5");var subQ2=makeQuery(id+"F0.imprint","INTERSECT",VERTEX,{"disambiguationData":[OD(0.0)],"derivedFrom":[subQ1,subQ0]});Q10=makeQuery(id+"F0.imprint","IMPRINT",FACE,{"disambiguationData":[TD([[makeQuery(id+"F0.imprint","IMPRINT",EDGE,{"disambiguationData":[TD([[subQ2,-1.0]])],"derivedFrom":subQ1}),-1.0]])]});}
            extrude(context, id + "F3", {"entities" : qUnion([Q0, Q1, Q2, Q3, Q4, Q5, Q6, Q7, Q8, Q9, Q10]), "endBound" : BoundingType.SYMMETRIC, "depth" : 2.8 * mm, "offsetDistance" : 25 * mm});
        }
        {
            var Q0;
            {var subQ0=sQuery(id+"F0.wireOp",EDGE,"E7");Q0=makeQuery(id+"F3.opExtrude","CAP_EDGE",EDGE,{"disambiguationData":[OSD([subQ0]),TDD([makeQuery(id+"F0.imprint","IMPRINT",EDGE,{"disambiguationData":[TD([[makeQuery(id+"F0.imprint","INTERSECT",VERTEX,{"disambiguationData":[OD(0.0)],"derivedFrom":[sQuery(id+"F0.wireOp",EDGE,"E5"),subQ0]}),1.0]])],"derivedFrom":subQ0})])],"isStart":false});}
            var Q1;
            {var subQ0=sQuery(id+"F0.wireOp",EDGE,"E7");Q1=makeQuery(id+"F3.opExtrude","CAP_EDGE",EDGE,{"disambiguationData":[OSD([subQ0]),TDD([makeQuery(id+"F0.imprint","IMPRINT",EDGE,{"disambiguationData":[TD([[makeQuery(id+"F0.imprint","INTERSECT",VERTEX,{"disambiguationData":[OD(1.0)],"derivedFrom":[sQuery(id+"F0.wireOp",EDGE,"E5"),subQ0]}),-1.0]])],"derivedFrom":subQ0})])],"isStart":false});}
            var Q2;
            {var subQ0=sQuery(id+"F0.wireOp",EDGE,"E8");Q2=makeQuery(id+"F3.opExtrude","CAP_EDGE",EDGE,{"disambiguationData":[OSD([subQ0]),TDD([makeQuery(id+"F0.imprint","IMPRINT",EDGE,{"disambiguationData":[TD([[makeQuery(id+"F0.imprint","INTERSECT",VERTEX,{"disambiguationData":[OD(1.0)],"derivedFrom":[sQuery(id+"F0.wireOp",EDGE,"E5"),subQ0]}),-1.0]])],"derivedFrom":subQ0})])],"isStart":false});}
            var Q3;
            {var subQ0=sQuery(id+"F0.wireOp",EDGE,"E8");Q3=makeQuery(id+"F3.opExtrude","CAP_EDGE",EDGE,{"disambiguationData":[OSD([subQ0]),TDD([makeQuery(id+"F0.imprint","IMPRINT",EDGE,{"disambiguationData":[TD([[makeQuery(id+"F0.imprint","INTERSECT",VERTEX,{"disambiguationData":[OD(1.0)],"derivedFrom":[sQuery(id+"F0.wireOp",EDGE,"E5"),subQ0]}),-1.0]])],"derivedFrom":subQ0})])],"isStart":true});}
            var Q4;
            {var subQ0=sQuery(id+"F0.wireOp",EDGE,"E7");Q4=makeQuery(id+"F3.opExtrude","CAP_EDGE",EDGE,{"disambiguationData":[OSD([subQ0]),TDD([makeQuery(id+"F0.imprint","IMPRINT",EDGE,{"disambiguationData":[TD([[makeQuery(id+"F0.imprint","INTERSECT",VERTEX,{"disambiguationData":[OD(0.0)],"derivedFrom":[sQuery(id+"F0.wireOp",EDGE,"E5"),subQ0]}),1.0]])],"derivedFrom":subQ0})])],"isStart":true});}
            var Q5;
            {var subQ0=sQuery(id+"F0.wireOp",EDGE,"E8");Q5=makeQuery(id+"F3.opExtrude","CAP_EDGE",EDGE,{"disambiguationData":[OSD([subQ0]),TDD([makeQuery(id+"F0.imprint","IMPRINT",EDGE,{"disambiguationData":[TD([[makeQuery(id+"F0.imprint","INTERSECT",VERTEX,{"disambiguationData":[OD(0.0)],"derivedFrom":[sQuery(id+"F0.wireOp",EDGE,"E5"),subQ0]}),1.0]])],"derivedFrom":subQ0})])],"isStart":true});}
            var Q6;
            {var subQ0=sQuery(id+"F0.wireOp",EDGE,"E7");Q6=makeQuery(id+"F3.opExtrude","CAP_EDGE",EDGE,{"disambiguationData":[OSD([subQ0]),TDD([makeQuery(id+"F0.imprint","IMPRINT",EDGE,{"disambiguationData":[TD([[makeQuery(id+"F0.imprint","INTERSECT",VERTEX,{"disambiguationData":[OD(1.0)],"derivedFrom":[sQuery(id+"F0.wireOp",EDGE,"E5"),subQ0]}),-1.0]])],"derivedFrom":subQ0})])],"isStart":true});}
            fillet(context, id + "F4", {"entities" : qUnion([Q0, Q1, Q2, Q3, Q4, Q5, Q6]), "radius" : 1 * mm, "tangentPropagation" : true, "allowEdgeOverflow" : false});
        }
        {
            var Q0;
            Q0=makeQuery(id+"F1.opExtrude","CAP_EDGE",EDGE,{"disambiguationData":[OSD([sQuery(id+"F0.wireOp",EDGE,"E4.4")])],"isStart":true});
            var Q1;
            Q1=makeQuery(id+"F1.opExtrude","CAP_EDGE",EDGE,{"disambiguationData":[OSD([sQuery(id+"F0.wireOp",EDGE,"E4.5")])],"isStart":true});
            var Q2;
            Q2=makeQuery(id+"F1.opExtrude","CAP_EDGE",EDGE,{"disambiguationData":[OSD([sQuery(id+"F0.wireOp",EDGE,"E4.0")])],"isStart":true});
            var Q3;
            Q3=makeQuery(id+"F1.opExtrude","CAP_EDGE",EDGE,{"disambiguationData":[OSD([sQuery(id+"F0.wireOp",EDGE,"E4.1")])],"isStart":true});
            var Q4;
            Q4=makeQuery(id+"F1.opExtrude","CAP_EDGE",EDGE,{"disambiguationData":[OSD([sQuery(id+"F0.wireOp",EDGE,"E4.2")])],"isStart":true});
            var Q5;
            Q5=makeQuery(id+"F1.opExtrude","CAP_EDGE",EDGE,{"disambiguationData":[OSD([sQuery(id+"F0.wireOp",EDGE,"E4.3")])],"isStart":true});
            var Q6;
            Q6=makeQuery(id+"F1.opExtrude","CAP_EDGE",EDGE,{"disambiguationData":[OSD([sQuery(id+"F0.wireOp",EDGE,"E3.5")])],"isStart":true});
            var Q7;
            Q7=makeQuery(id+"F1.opExtrude","CAP_EDGE",EDGE,{"disambiguationData":[OSD([sQuery(id+"F0.wireOp",EDGE,"E3.0")])],"isStart":true});
            var Q8;
            Q8=makeQuery(id+"F1.opExtrude","CAP_EDGE",EDGE,{"disambiguationData":[OSD([sQuery(id+"F0.wireOp",EDGE,"E3.1")])],"isStart":true});
            var Q9;
            Q9=makeQuery(id+"F1.opExtrude","CAP_EDGE",EDGE,{"disambiguationData":[OSD([sQuery(id+"F0.wireOp",EDGE,"E4.0")])],"isStart":false});
            var Q10;
            Q10=makeQuery(id+"F1.opExtrude","CAP_EDGE",EDGE,{"disambiguationData":[OSD([sQuery(id+"F0.wireOp",EDGE,"E4.1")])],"isStart":false});
            var Q11;
            Q11=makeQuery(id+"F1.opExtrude","CAP_EDGE",EDGE,{"disambiguationData":[OSD([sQuery(id+"F0.wireOp",EDGE,"E4.2")])],"isStart":false});
            var Q12;
            Q12=makeQuery(id+"F1.opExtrude","CAP_EDGE",EDGE,{"disambiguationData":[OSD([sQuery(id+"F0.wireOp",EDGE,"E4.3")])],"isStart":false});
            var Q13;
            Q13=makeQuery(id+"F1.opExtrude","CAP_EDGE",EDGE,{"disambiguationData":[OSD([sQuery(id+"F0.wireOp",EDGE,"E4.4")])],"isStart":false});
            var Q14;
            Q14=makeQuery(id+"F1.opExtrude","CAP_EDGE",EDGE,{"disambiguationData":[OSD([sQuery(id+"F0.wireOp",EDGE,"E4.5")])],"isStart":false});
            var Q15;
            Q15=makeQuery(id+"F1.opExtrude","CAP_EDGE",EDGE,{"disambiguationData":[OSD([sQuery(id+"F0.wireOp",EDGE,"E3.1")])],"isStart":false});
            var Q16;
            Q16=makeQuery(id+"F1.opExtrude","CAP_EDGE",EDGE,{"disambiguationData":[OSD([sQuery(id+"F0.wireOp",EDGE,"mRkxw26x-I3Gl-08el-Mtzy-OSO2PS5uUvGy")])],"isStart":false});
            var Q17;
            Q17=makeQuery(id+"F1.opExtrude","CAP_EDGE",EDGE,{"disambiguationData":[OSD([sQuery(id+"F0.wireOp",EDGE,"E3.5")])],"isStart":false});
            var Q18;
            Q18=makeQuery(id+"F1.opExtrude","CAP_EDGE",EDGE,{"disambiguationData":[OSD([sQuery(id+"F0.wireOp",EDGE,"E3.0")])],"isStart":false});
            var Q19;
            Q19=makeQuery(id+"F1.opExtrude","CAP_EDGE",EDGE,{"disambiguationData":[OSD([sQuery(id+"F0.wireOp",EDGE,"E3.4")])],"isStart":true});
            var Q20;
            Q20=makeQuery(id+"F1.opExtrude","CAP_EDGE",EDGE,{"disambiguationData":[OSD([sQuery(id+"F0.wireOp",EDGE,"E9")])],"isStart":true});
            var Q21;
            Q21=makeQuery(id+"F1.opExtrude","CAP_EDGE",EDGE,{"disambiguationData":[OSD([sQuery(id+"F0.wireOp",EDGE,"E9")])],"isStart":false});
            var Q22;
            Q22=makeQuery(id+"F1.opExtrude","CAP_EDGE",EDGE,{"disambiguationData":[OSD([sQuery(id+"F0.wireOp",EDGE,"E3.4")])],"isStart":false});
            chamfer(context, id + "F5", {"entities" : qUnion([Q0, Q1, Q2, Q3, Q4, Q5, Q6, Q7, Q8, Q9, Q10, Q11, Q12, Q13, Q14, Q15, Q16, Q17, Q18, Q19, Q20, Q21, Q22]), "width" : 0.8 * mm, "tangentPropagation" : true});
        }
        {
            var Q0;
            Q0=makeQuery(id+"F1.opExtrude","CAP_EDGE",EDGE,{"disambiguationData":[OSD([sQuery(id+"F0.wireOp",EDGE,"E5")])],"isStart":false});
            var Q1;
            Q1=makeQuery(id+"F1.opExtrude","CAP_EDGE",EDGE,{"disambiguationData":[OSD([sQuery(id+"F0.wireOp",EDGE,"E5")])],"isStart":true});
            var Q2;
            Q2=makeQuery(id+"F1.opExtrude","CAP_EDGE",EDGE,{"disambiguationData":[OSD([sQuery(id+"F0.wireOp",EDGE,"E6")])],"isStart":false});
            var Q3;
            Q3=makeQuery(id+"F1.opExtrude","CAP_EDGE",EDGE,{"disambiguationData":[OSD([sQuery(id+"F0.wireOp",EDGE,"E6")])],"isStart":true});
            fillet(context, id + "F6", {"entities" : qUnion([Q0, Q1, Q2, Q3]), "radius" : 3 * mm, "tangentPropagation" : true, "allowEdgeOverflow" : false});
        }
        {
            var Q0;
            Q0=makeQuery(id+"F2.opExtrude","CAP_EDGE",EDGE,{"disambiguationData":[OSD([sQuery(id+"F0.wireOp",EDGE,"E5")])],"isStart":false});
            var Q1;
            Q1=makeQuery(id+"F2.opExtrude","CAP_EDGE",EDGE,{"disambiguationData":[OSD([sQuery(id+"F0.wireOp",EDGE,"E6")])],"isStart":false});
            var Q2;
            Q2=makeQuery(id+"F2.opExtrude","CAP_EDGE",EDGE,{"disambiguationData":[OSD([sQuery(id+"F0.wireOp",EDGE,"E6")])],"isStart":true});
            var Q3;
            Q3=makeQuery(id+"F2.opExtrude","CAP_EDGE",EDGE,{"disambiguationData":[OSD([sQuery(id+"F0.wireOp",EDGE,"E5")])],"isStart":true});
            var Q4;
            {var subQ0=sQuery(id+"F0.wireOp",EDGE,"E5");var subQ1=sQuery(id+"F0.wireOp",EDGE,"E1");Q4=makeQuery(id+"F2.opExtrude","SWEPT_EDGE",EDGE,{"disambiguationData":[OSD([subQ1,subQ0]),TDD([makeQuery(id+"F0.imprint","INTERSECT",VERTEX,{"disambiguationData":[OD(0.0)],"derivedFrom":[subQ1,subQ0]})])]});}
            var Q5;
            {var subQ0=sQuery(id+"F0.wireOp",EDGE,"E5");var subQ1=sQuery(id+"F0.wireOp",EDGE,"E1");Q5=makeQuery(id+"F2.opExtrude","SWEPT_EDGE",EDGE,{"disambiguationData":[OSD([subQ1,subQ0]),TDD([makeQuery(id+"F0.imprint","INTERSECT",VERTEX,{"disambiguationData":[OD(1.0)],"derivedFrom":[subQ1,subQ0]})])]});}
            var Q6;
            {var subQ0=sQuery(id+"F0.wireOp",EDGE,"E6");var subQ1=sQuery(id+"F0.wireOp",EDGE,"E1");Q6=makeQuery(id+"F2.opExtrude","SWEPT_EDGE",EDGE,{"disambiguationData":[OSD([subQ1,subQ0]),TDD([makeQuery(id+"F0.imprint","INTERSECT",VERTEX,{"disambiguationData":[OD(0.0)],"derivedFrom":[subQ1,subQ0]})])]});}
            var Q7;
            {var subQ0=sQuery(id+"F0.wireOp",EDGE,"E6");var subQ1=sQuery(id+"F0.wireOp",EDGE,"E1");Q7=makeQuery(id+"F2.opExtrude","SWEPT_EDGE",EDGE,{"disambiguationData":[OSD([subQ1,subQ0]),TDD([makeQuery(id+"F0.imprint","INTERSECT",VERTEX,{"disambiguationData":[OD(1.0)],"derivedFrom":[subQ1,subQ0]})])]});}
            fillet(context, id + "F7", {"entities" : qUnion([Q0, Q1, Q2, Q3, Q4, Q5, Q6, Q7]), "radius" : 1.5 * mm, "tangentPropagation" : true, "allowEdgeOverflow" : false});
        }
        {
            var Q0;
            {var subQ0=sQuery(id+"F0.wireOp",EDGE,"E12.top");var subQ1=sQuery(id+"F0.wireOp",EDGE,"E1");var subQ2=makeQuery(id+"F0.imprint","INTERSECT",VERTEX,{"disambiguationData":[OD(1.0)],"derivedFrom":[subQ1,subQ0]});var subQ3=makeQuery(id+"F0.imprint","INTERSECT",VERTEX,{"disambiguationData":[OD(0.0)],"derivedFrom":[subQ1,subQ0]});Q0=makeQuery(id+"F2.opExtrude","CAP_EDGE",EDGE,{"disambiguationData":[OSD([subQ1]),TDD([makeQuery(id+"F0.imprint","IMPRINT",EDGE,{"disambiguationData":[TD([[makeQuery(id+"F0.imprint","INTERSECT",VERTEX,{"disambiguationData":[OD(1.0)],"derivedFrom":[subQ1,sQuery(id+"F0.wireOp",EDGE,"E5")]}),-1.0]])],"derivedFrom":subQ1}),makeQuery(id+"F0.imprint","IMPRINT",EDGE,{"disambiguationData":[TD([[subQ3,-1.0]])],"derivedFrom":subQ1}),makeQuery(id+"F0.imprint","IMPRINT",EDGE,{"disambiguationData":[TD([[subQ2,-1.0]])],"derivedFrom":subQ1})])],"isStart":false});}
            var Q1;
            {var subQ0=sQuery(id+"F0.wireOp",EDGE,"E12.bottom");var subQ1=sQuery(id+"F0.wireOp",EDGE,"E1");var subQ2=makeQuery(id+"F0.imprint","INTERSECT",VERTEX,{"disambiguationData":[OD(1.0)],"derivedFrom":[subQ1,subQ0]});var subQ3=makeQuery(id+"F0.imprint","INTERSECT",VERTEX,{"disambiguationData":[OD(0.0)],"derivedFrom":[subQ1,subQ0]});Q1=makeQuery(id+"F2.opExtrude","CAP_EDGE",EDGE,{"disambiguationData":[OSD([subQ1]),TDD([makeQuery(id+"F0.imprint","IMPRINT",EDGE,{"disambiguationData":[TD([[makeQuery(id+"F0.imprint","INTERSECT",VERTEX,{"disambiguationData":[OD(0.0)],"derivedFrom":[subQ1,sQuery(id+"F0.wireOp",EDGE,"E6")]}),-1.0]])],"derivedFrom":subQ1}),makeQuery(id+"F0.imprint","IMPRINT",EDGE,{"disambiguationData":[TD([[subQ3,-1.0]])],"derivedFrom":subQ1}),makeQuery(id+"F0.imprint","IMPRINT",EDGE,{"disambiguationData":[TD([[subQ2,-1.0]])],"derivedFrom":subQ1})])],"isStart":false});}
            var Q2;
            {var subQ0=sQuery(id+"F0.wireOp",EDGE,"E12.top");var subQ1=sQuery(id+"F0.wireOp",EDGE,"E1");var subQ2=makeQuery(id+"F0.imprint","INTERSECT",VERTEX,{"disambiguationData":[OD(1.0)],"derivedFrom":[subQ1,subQ0]});var subQ3=makeQuery(id+"F0.imprint","INTERSECT",VERTEX,{"disambiguationData":[OD(0.0)],"derivedFrom":[subQ1,subQ0]});Q2=makeQuery(id+"F2.opExtrude","CAP_EDGE",EDGE,{"disambiguationData":[OSD([subQ1]),TDD([makeQuery(id+"F0.imprint","IMPRINT",EDGE,{"disambiguationData":[TD([[makeQuery(id+"F0.imprint","INTERSECT",VERTEX,{"disambiguationData":[OD(1.0)],"derivedFrom":[subQ1,sQuery(id+"F0.wireOp",EDGE,"E5")]}),-1.0]])],"derivedFrom":subQ1}),makeQuery(id+"F0.imprint","IMPRINT",EDGE,{"disambiguationData":[TD([[subQ3,-1.0]])],"derivedFrom":subQ1}),makeQuery(id+"F0.imprint","IMPRINT",EDGE,{"disambiguationData":[TD([[subQ2,-1.0]])],"derivedFrom":subQ1})])],"isStart":true});}
            var Q3;
            {var subQ0=sQuery(id+"F0.wireOp",EDGE,"E12.bottom");var subQ1=sQuery(id+"F0.wireOp",EDGE,"E1");var subQ2=makeQuery(id+"F0.imprint","INTERSECT",VERTEX,{"disambiguationData":[OD(1.0)],"derivedFrom":[subQ1,subQ0]});var subQ3=makeQuery(id+"F0.imprint","INTERSECT",VERTEX,{"disambiguationData":[OD(0.0)],"derivedFrom":[subQ1,subQ0]});Q3=makeQuery(id+"F2.opExtrude","CAP_EDGE",EDGE,{"disambiguationData":[OSD([subQ1]),TDD([makeQuery(id+"F0.imprint","IMPRINT",EDGE,{"disambiguationData":[TD([[makeQuery(id+"F0.imprint","INTERSECT",VERTEX,{"disambiguationData":[OD(0.0)],"derivedFrom":[subQ1,sQuery(id+"F0.wireOp",EDGE,"E6")]}),-1.0]])],"derivedFrom":subQ1}),makeQuery(id+"F0.imprint","IMPRINT",EDGE,{"disambiguationData":[TD([[subQ3,-1.0]])],"derivedFrom":subQ1}),makeQuery(id+"F0.imprint","IMPRINT",EDGE,{"disambiguationData":[TD([[subQ2,-1.0]])],"derivedFrom":subQ1})])],"isStart":true});}
            fillet(context, id + "F8", {"entities" : qUnion([Q0, Q1, Q2, Q3]), "radius" : 3 * mm, "tangentPropagation" : true, "allowEdgeOverflow" : false});
        }
        {
            var Q0;
            {var subQ0=sQuery(id+"F0.wireOp",EDGE,"E18");var subQ1=makeQuery(id+"F0.imprint","INTERSECT",VERTEX,{"disambiguationData":[OD(1.0)],"derivedFrom":[sQuery(id+"F0.wireOp",EDGE,"E17"),subQ0]});Q0=makeQuery(id+"F3.opExtrude","CAP_EDGE",EDGE,{"disambiguationData":[OSD([subQ0]),TDD([makeQuery(id+"F0.imprint","IMPRINT",EDGE,{"disambiguationData":[TD([[subQ1,1.0]])],"derivedFrom":subQ0}),makeQuery(id+"F0.imprint","IMPRINT",EDGE,{"disambiguationData":[TD([[makeQuery(id+"F0.imprint","INTERSECT",VERTEX,{"disambiguationData":[OD(1.0)],"derivedFrom":[sQuery(id+"F0.wireOp",EDGE,"E6"),subQ0]}),1.0]])],"derivedFrom":subQ0})])],"isStart":true});}
            var Q1;
            {var subQ0=sQuery(id+"F0.wireOp",EDGE,"E18");var subQ1=makeQuery(id+"F0.imprint","INTERSECT",VERTEX,{"disambiguationData":[OD(1.0)],"derivedFrom":[sQuery(id+"F0.wireOp",EDGE,"E17"),subQ0]});Q1=makeQuery(id+"F3.opExtrude","CAP_EDGE",EDGE,{"disambiguationData":[OSD([subQ0]),TDD([makeQuery(id+"F0.imprint","IMPRINT",EDGE,{"disambiguationData":[TD([[subQ1,1.0]])],"derivedFrom":subQ0}),makeQuery(id+"F0.imprint","IMPRINT",EDGE,{"disambiguationData":[TD([[makeQuery(id+"F0.imprint","INTERSECT",VERTEX,{"disambiguationData":[OD(1.0)],"derivedFrom":[sQuery(id+"F0.wireOp",EDGE,"E6"),subQ0]}),1.0]])],"derivedFrom":subQ0})])],"isStart":false});}
            var Q2;
            {var subQ0=sQuery(id+"F0.wireOp",EDGE,"E17");var subQ1=makeQuery(id+"F0.imprint","INTERSECT",VERTEX,{"disambiguationData":[OD(0.0)],"derivedFrom":[subQ0,sQuery(id+"F0.wireOp",EDGE,"E18")]});Q2=makeQuery(id+"F3.opExtrude","CAP_EDGE",EDGE,{"disambiguationData":[OSD([subQ0]),TDD([makeQuery(id+"F0.imprint","IMPRINT",EDGE,{"disambiguationData":[TD([[subQ1,1.0]])],"derivedFrom":subQ0}),makeQuery(id+"F0.imprint","IMPRINT",EDGE,{"disambiguationData":[TD([[makeQuery(id+"F0.imprint","INTERSECT",VERTEX,{"disambiguationData":[OD(0.0)],"derivedFrom":[sQuery(id+"F0.wireOp",EDGE,"E5"),subQ0]}),1.0]])],"derivedFrom":subQ0})])],"isStart":true});}
            var Q3;
            {var subQ0=sQuery(id+"F0.wireOp",EDGE,"E17");var subQ1=makeQuery(id+"F0.imprint","INTERSECT",VERTEX,{"disambiguationData":[OD(0.0)],"derivedFrom":[subQ0,sQuery(id+"F0.wireOp",EDGE,"E18")]});Q3=makeQuery(id+"F3.opExtrude","CAP_EDGE",EDGE,{"disambiguationData":[OSD([subQ0]),TDD([makeQuery(id+"F0.imprint","IMPRINT",EDGE,{"disambiguationData":[TD([[subQ1,1.0]])],"derivedFrom":subQ0}),makeQuery(id+"F0.imprint","IMPRINT",EDGE,{"disambiguationData":[TD([[makeQuery(id+"F0.imprint","INTERSECT",VERTEX,{"disambiguationData":[OD(0.0)],"derivedFrom":[sQuery(id+"F0.wireOp",EDGE,"E5"),subQ0]}),1.0]])],"derivedFrom":subQ0})])],"isStart":false});}
            chamfer(context, id + "F9", {"entities" : qUnion([Q0, Q1, Q2, Q3]), "width" : 0.4 * mm, "tangentPropagation" : true});
        }
    });
